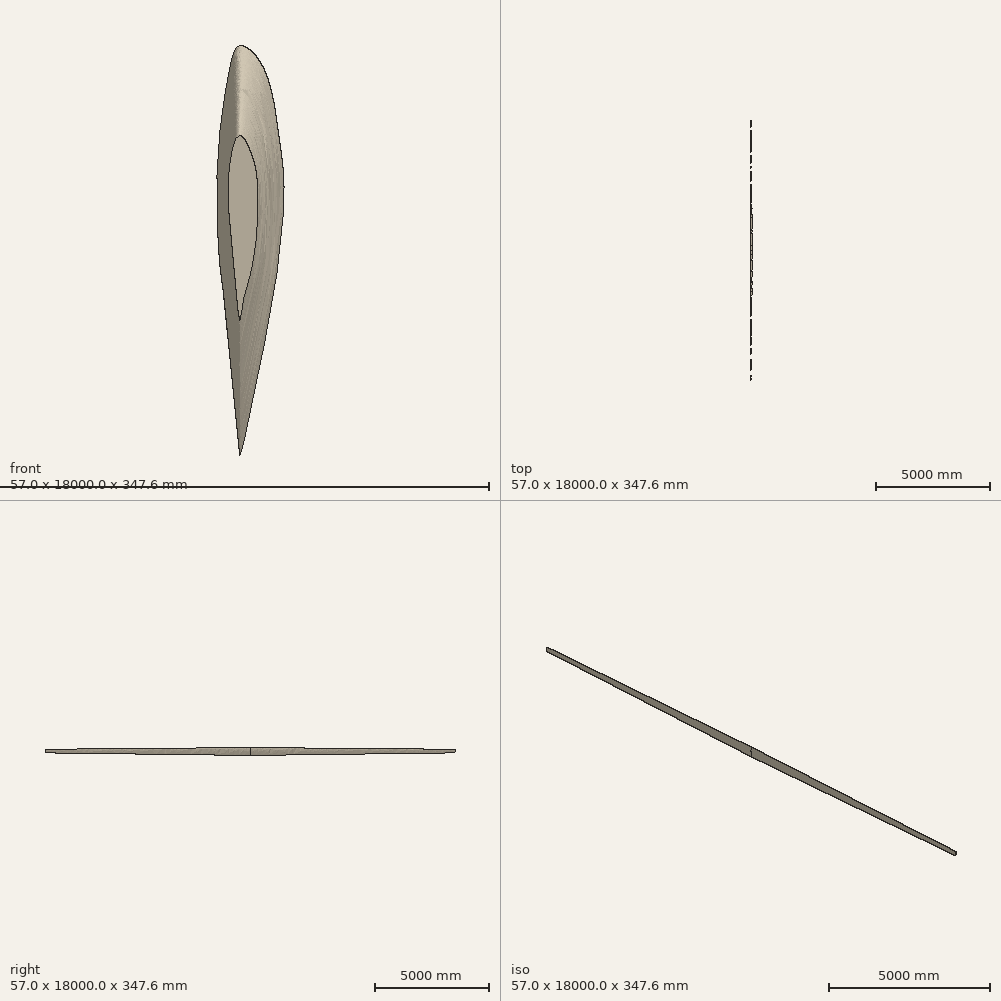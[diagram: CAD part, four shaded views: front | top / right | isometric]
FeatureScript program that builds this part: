
annotation { "Feature Type Name" : "Feature", "Feature Type Description" : "" }
export const myFeature = defineFeature(function(context is Context, id is Id, definition is map)
    precondition{}
    {
        {
            var Q0;
            Q0=qCreatedBy(makeId("Front.planeOp"),FACE);
            var sketch = newSketch(context, id + "F0", { "sketchPlane" : qUnion([Q0])});
            skLineSegment(sketch, "E0", {"start": v(0, 0) * mm, "end": v(304.5, 0) * mm, "construction": true});
            skLineSegment(sketch, "E1", {"start": v(0, 0) * mm, "end": v(-304.5, 0) * mm, "construction": true});
            skLineSegment(sketch, "E2", {"start": v(0, 0) * mm, "end": v(0, -411.95) * mm, "construction": true});
            skFitSpline(sketch, "E3", {"points": [v(0, 119.65) * mm, v(14.2, 110.38) * mm, v(25.74, 85.52) * mm, v(33.93, 41.22) * mm, v(37.3, -16.76) * mm, v(25.72, -109) * mm, v(13.85, -166.4) * mm, v(0, -227.75) * mm, v(0, -159.16) * mm, v(-13.84, -88.73) * mm, v(-19.04, -29.84) * mm, v(-18.36, 31.15) * mm, v(-9.96, 93.3) * mm, v(0, 119.65) * mm]});
            skSolve(sketch);
        }
        {
            var Q0;
            Q0=qCreatedBy(makeId("Front.planeOp"),FACE);
            cPlane(context, id + "F1", {"entities" : qUnion([Q0]), "cplaneType" : CPlaneType.OFFSET, "offset" : 9000 * mm, "width" : 152.4 * mm, "height" : 152.4 * mm});
        }
        {
            var Q0;
            Q0=qCreatedBy(id+"F1.planeOp",FACE);
            var sketch = newSketch(context, id + "F2", { "sketchPlane" : qUnion([Q0])});
            skFitSpline(sketch, "E4", {"points": [v(0, 44.26) * mm, v(8.87, 30.65) * mm, v(14.31, 10.04) * mm, v(15.48, -18.74) * mm, v(13.53, -48.68) * mm, v(8.1, -77.84) * mm, v(3.03, -96.5) * mm, v(0, -114) * mm, v(-3.58, -81.34) * mm, v(-6.69, -51.79) * mm, v(-9.4, -21.46) * mm, v(-9.4, 10.04) * mm, v(-5.13, 35.7) * mm, v(0, 44.26) * mm]});
            skSolve(sketch);
        }
        {
            var Q0;
            Q0=sQuery(id+"F0.wireOp",VERTEX,"E3.7.internal");
            var Q1;
            Q1=sQuery(id+"F2.wireOp",VERTEX,"E4.7.internal");
            var Q2;
            Q2=sQuery(id+"F0.wireOp",VERTEX,"E3.0.internal");
            cPlane(context, id + "F3", {"entities" : qUnion([Q0, Q1, Q2]), "cplaneType" : CPlaneType.THREE_POINT, "offset" : 152.4 * mm, "width" : 152.4 * mm, "height" : 152.4 * mm});
        }
        {
            var Q0;
            Q0=qCreatedBy(id+"F3.planeOp",FACE);
            var sketch = newSketch(context, id + "F4", { "sketchPlane" : qUnion([Q0])});
            skPoint(sketch, "E5.0", {"position": v(-9000, -114) * mm});
            skPoint(sketch, "E6.0", {"position": v(0, -227.75) * mm});
            skLineSegment(sketch, "E7", {"start": v(0, -227.75) * mm, "end": v(-9000, -114) * mm});
            skSolve(sketch);
        }
        {
            var Q0;
            Q0=makeQuery(id+"F2.imprint","IMPRINT",FACE,{"disambiguationData":[TD([[makeQuery(id+"F2.imprint","IMPRINT",EDGE,{"derivedFrom":sQuery(id+"F2.wireOp",EDGE,"E4")}),-1.0]])]});
            var Q1;
            Q1=makeQuery(id+"F0.imprint","IMPRINT",FACE,{"disambiguationData":[TD([[makeQuery(id+"F0.imprint","IMPRINT",EDGE,{"derivedFrom":sQuery(id+"F0.wireOp",EDGE,"E3")}),-1.0]])]});
            var Q2;
            Q2=sQuery(id+"F4.wireOp",EDGE,"E7");
            loft(context, id + "F5", {"addGuides" : true, "sheetProfilesArray" : [{ "sheetProfileEntities" : qUnion([Q0]) }, { "sheetProfileEntities" : qUnion([Q1]) }], "guidesArray" : [{ "guideEntities" : qUnion([Q2]), "guideDerivativeType" : LoftGuideDerivativeType.DEFAULT, "guideDerivativeMagnitude" : 1 }]});
        }
        {
            var Q0;
            Q0=makeQuery(id+"F5.opLoft","SWEPT_BODY",BODY,{"disambiguationData":[OSD([makeQuery(id+"F0.imprint","IMPRINT",FACE,{"disambiguationData":[TD([[makeQuery(id+"F0.imprint","IMPRINT",EDGE,{"derivedFrom":sQuery(id+"F0.wireOp",EDGE,"E3")}),-1.0]])]}),makeQuery(id+"F2.imprint","IMPRINT",FACE,{"disambiguationData":[TD([[makeQuery(id+"F2.imprint","IMPRINT",EDGE,{"derivedFrom":sQuery(id+"F2.wireOp",EDGE,"E4")}),-1.0]])]}),sQuery(id+"F4.wireOp",EDGE,"E7")])]});
            var Q1;
            Q1=makeQuery(id+"F5.opLoft","CAP_FACE",FACE,{"disambiguationData":[OSD([makeQuery(id+"F0.imprint","IMPRINT",FACE,{"disambiguationData":[TD([[makeQuery(id+"F0.imprint","IMPRINT",EDGE,{"derivedFrom":sQuery(id+"F0.wireOp",EDGE,"E3")}),-1.0]])]})])],"isStart":true});
            mirror(context, id + "F7", {"operationType" : NewBodyOperationType.ADD, "entities" : qUnion([Q0]), "mirrorPlane" : qUnion([Q1])});
        }
    });
